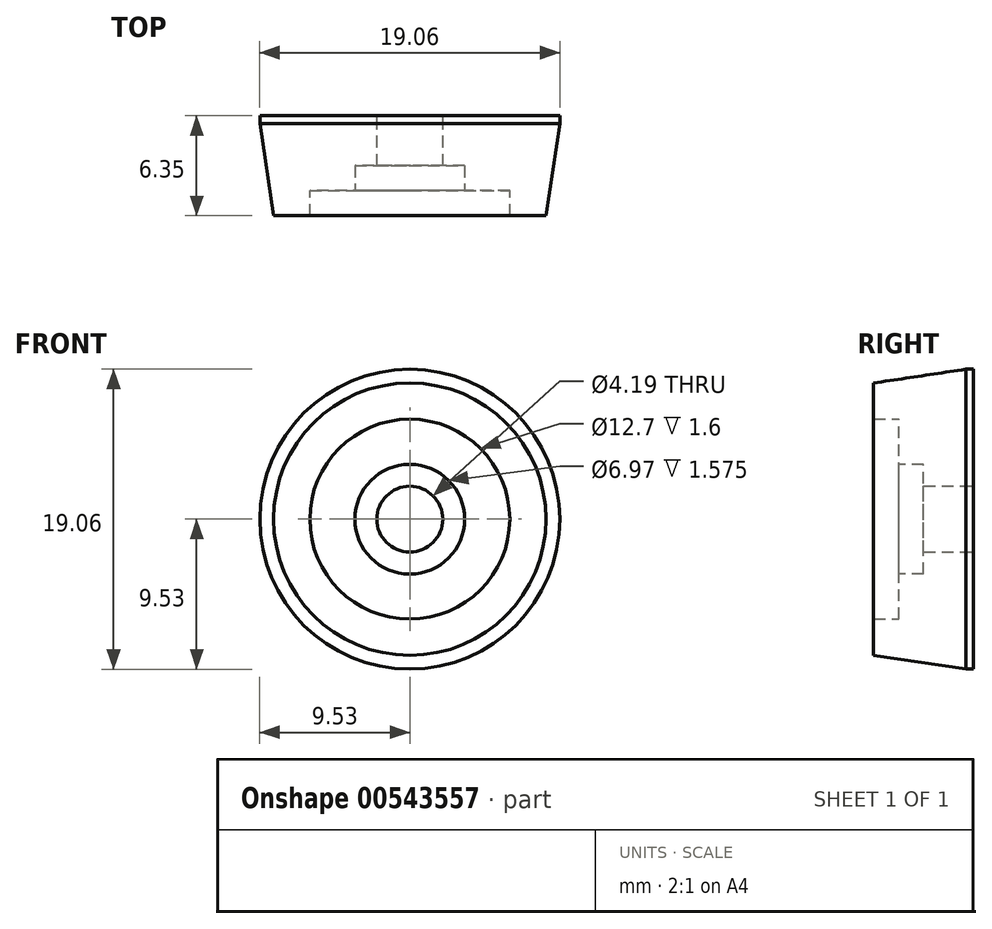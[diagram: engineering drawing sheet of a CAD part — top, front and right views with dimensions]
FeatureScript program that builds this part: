
annotation { "Feature Type Name" : "Feature", "Feature Type Description" : "" }
export const myFeature = defineFeature(function(context is Context, id is Id, definition is map)
    precondition{}
    {
        {
            var Q0;
            Q0=qCreatedBy(makeId("Front.planeOp"),FACE);
            var sketch = newSketch(context, id + "F0", { "sketchPlane" : qUnion([Q0])});
            skCircle(sketch, "E0", {"center": v(0, 0) * mm, "radius": 9.53 * mm});
            skCircle(sketch, "E1.0", {"center": v(0, 0) * mm, "radius": 6.35 * mm});
            skCircle(sketch, "E2", {"center": v(0, 0) * mm, "radius": 2.1 * mm});
            skCircle(sketch, "E3", {"center": v(0, 0) * mm, "radius": 3.49 * mm});
            skSolve(sketch);
        }
        {
            var Q0;
            Q0=makeQuery(id+"F0.imprint","IMPRINT",FACE,{"disambiguationData":[TD([[makeQuery(id+"F0.imprint","IMPRINT",EDGE,{"derivedFrom":sQuery(id+"F0.wireOp",EDGE,"E0")}),1.0]])]});
            extrude(context, id + "F1", {"entities" : qUnion([Q0]), "depth" : 3.17 * mm, "offsetDistance" : 25.4 * mm});
        }
        {
            var Q0;
            Q0=makeQuery(id+"F0.imprint","IMPRINT",FACE,{"disambiguationData":[TD([[makeQuery(id+"F0.imprint","IMPRINT",EDGE,{"derivedFrom":sQuery(id+"F0.wireOp",EDGE,"E1.0")}),1.0]])]});
            extrude(context, id + "F2", {"entities" : qUnion([Q0]), "operationType" : NewBodyOperationType.ADD, "depth" : 4.75 * mm, "offsetDistance" : 25.4 * mm});
        }
        {
            var Q0;
            Q0=qCreatedBy(makeId("Right.planeOp"),FACE);
            var sketch = newSketch(context, id + "F3", { "sketchPlane" : qUnion([Q0])});
            skLineSegment(sketch, "E4", {"start": v(0, 9.6) * mm, "end": v(-7.97, 8.4) * mm});
            skLineSegment(sketch, "E5", {"start": v(-7.97, 8.4) * mm, "end": v(-7.97, 9.66) * mm});
            skLineSegment(sketch, "E6", {"start": v(-7.97, 9.66) * mm, "end": v(0, 9.66) * mm});
            skLineSegment(sketch, "E7", {"start": v(0, 9.66) * mm, "end": v(0, 9.6) * mm});
            skSolve(sketch);
        }
        {
            var Q0;
            Q0 = qSketchRegion(id + "F0", true);
            var Q1;
            Q1=makeQuery(id+"F0.imprint","IMPRINT",FACE,{"disambiguationData":[TD([[makeQuery(id+"F0.imprint","IMPRINT",EDGE,{"derivedFrom":sQuery(id+"F0.wireOp",EDGE,"E2")}),-1.0]])]});
            extrude(context, id + "F4", {"entities" : qUnion([Q0, Q1]), "operationType" : NewBodyOperationType.ADD, "depth" : 6.35 * mm, "offsetDistance" : 25.4 * mm});
        }
        {
            var Q0;
            Q0=makeQuery(id+"F4.opExtrude","CAP_FACE",FACE,{"disambiguationData":[OSD([sQuery(id+"F0.wireOp",EDGE,"E2"),sQuery(id+"F0.wireOp",EDGE,"E3")])],"isStart":false});
            extrude(context, id + "F5", {"entities" : qUnion([Q0]), "operationType" : NewBodyOperationType.REMOVE, "oppositeDirection" : true, "depth" : 3.17 * mm, "offsetDistance" : 25.4 * mm});
        }
        {
            var Q0;
            Q0 = qSketchRegion(id + "F3", true);
            var Q1;
            Q1=makeQuery(id+"F5.boolean.opBoolean","COPY",FACE,{"derivedFrom":makeQuery(id+"F5.opExtrude","SWEPT_FACE",FACE,{"disambiguationData":[OSD([sQuery(id+"F0.wireOp",EDGE,"E3")])]})});
            revolve(context, id + "F6", {"operationType" : NewBodyOperationType.REMOVE, "entities" : qUnion([Q0]), "axis" : qUnion([Q1]), "revolveType" : RevolveType.FULL, "oppositeDirection" : true});
        }
    });
